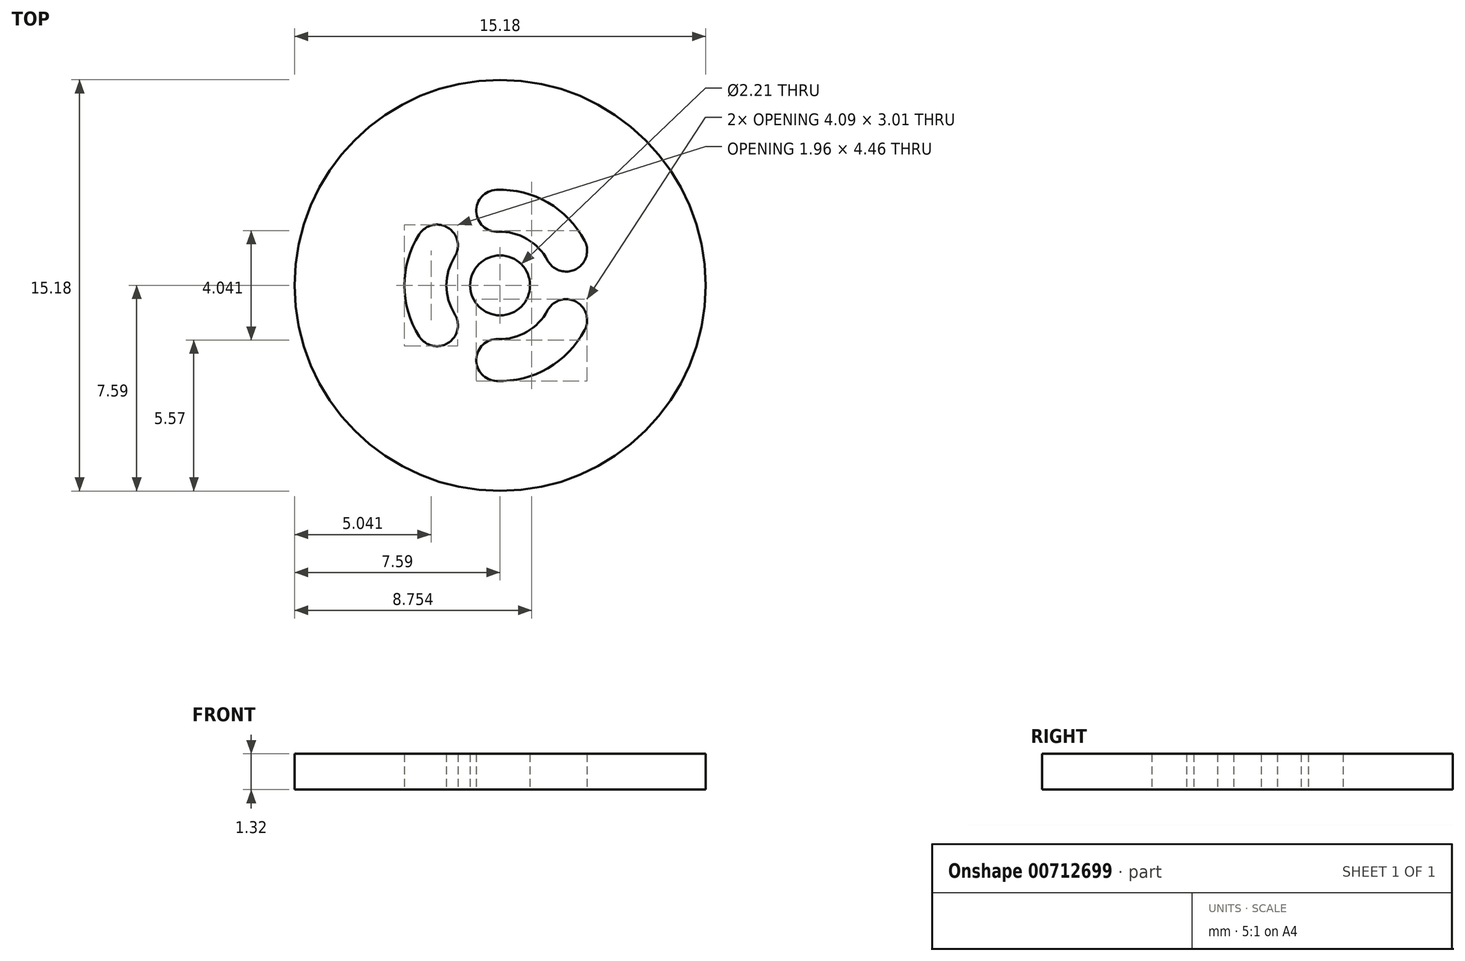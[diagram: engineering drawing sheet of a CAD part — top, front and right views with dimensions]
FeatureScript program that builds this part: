
annotation { "Feature Type Name" : "Feature", "Feature Type Description" : "" }
export const myFeature = defineFeature(function(context is Context, id is Id, definition is map)
    precondition{}
    {
        {
            var Q0;
            Q0=qCreatedBy(makeId("Top.planeOp"),FACE);
            var sketch = newSketch(context, id + "F0", { "sketchPlane" : qUnion([Q0])});
            skCircle(sketch, "E0", {"center": v(0, 0) * mm, "radius": 7.59 * mm});
            skCircle(sketch, "E1", {"center": v(0, 0) * mm, "radius": 1.1 * mm});
            skArc(sketch, "E2", {"start": v(1.75, 0.92) * mm, "mid": v(0.99, 1.71) * mm, "end": v(-0.08, 1.98) * mm});
            skArc(sketch, "E3", {"start": v(3.12, 1.65) * mm, "mid": v(1.76, 3.06) * mm, "end": v(-0.14, 3.53) * mm});
            skArc(sketch, "E4", {"start": v(1.75, 0.92) * mm, "mid": v(2.8, 0.6) * mm, "end": v(3.12, 1.65) * mm});
            skArc(sketch, "E5.MirrorC", {"start": v(1.75, -0.92) * mm, "mid": v(2.8, -0.6) * mm, "end": v(3.12, -1.65) * mm});
            skArc(sketch, "E6.1.0", {"start": v(-1.68, 1.06) * mm, "mid": v(-1.92, 2.12) * mm, "end": v(-2.99, 1.88) * mm});
            skArc(sketch, "E6.2.0", {"start": v(-0.08, -1.98) * mm, "mid": v(-0.88, -2.72) * mm, "end": v(-0.14, -3.53) * mm});
            skArc(sketch, "E7.1.0", {"start": v(-0.08, 1.98) * mm, "mid": v(-0.88, 2.72) * mm, "end": v(-0.14, 3.53) * mm});
            skArc(sketch, "E7.2.0", {"start": v(-1.68, -1.06) * mm, "mid": v(-1.92, -2.12) * mm, "end": v(-2.99, -1.88) * mm});
            skArc(sketch, "E8.trimOffspring", {"start": v(-1.68, 1.06) * mm, "mid": v(-1.98, 0) * mm, "end": v(-1.68, -1.06) * mm});
            skArc(sketch, "E9.trimOffspring", {"start": v(-2.99, 1.88) * mm, "mid": v(-3.53, 0) * mm, "end": v(-2.99, -1.88) * mm});
            skArc(sketch, "E10.trimOffspring", {"start": v(-0.14, -3.53) * mm, "mid": v(1.76, -3.06) * mm, "end": v(3.12, -1.65) * mm});
            skArc(sketch, "E11.trimOffspring", {"start": v(-0.08, -1.98) * mm, "mid": v(0.99, -1.71) * mm, "end": v(1.75, -0.92) * mm});
            skSolve(sketch);
        }
        {
            var Q0;
            Q0=makeQuery(id+"F0.imprint","IMPRINT",FACE,{"disambiguationData":[TD([[makeQuery(id+"F0.imprint","IMPRINT",EDGE,{"derivedFrom":sQuery(id+"F0.wireOp",EDGE,"E0")}),1.0]])]});
            extrude(context, id + "F1", {"entities" : qUnion([Q0]), "depth" : 1.32 * mm, "offsetDistance" : 25 * mm});
        }
    });
